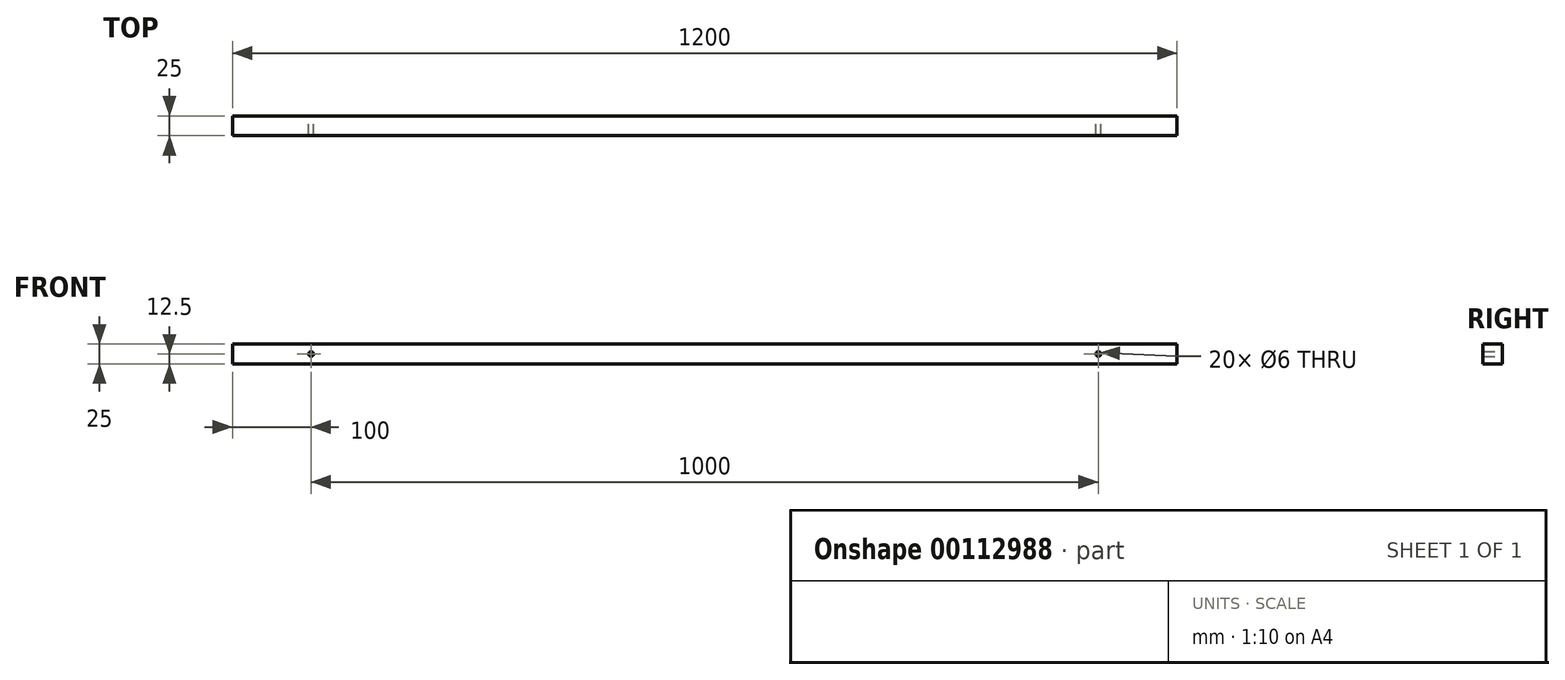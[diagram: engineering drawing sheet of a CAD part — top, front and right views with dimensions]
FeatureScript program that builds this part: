
annotation { "Feature Type Name" : "Feature", "Feature Type Description" : "" }
export const myFeature = defineFeature(function(context is Context, id is Id, definition is map)
    precondition{}
    {
        {
            var Q0;
            Q0=qCreatedBy(makeId("Front.planeOp"),FACE);
            var sketch = newSketch(context, id + "F0", { "sketchPlane" : qUnion([Q0])});
            skLineSegment(sketch, "E0.bottom", {"start": v(600, 12.5) * mm, "end": v(-600, 12.5) * mm});
            skLineSegment(sketch, "E0.top", {"start": v(600, -12.5) * mm, "end": v(-600, -12.5) * mm});
            skLineSegment(sketch, "E0.left", {"start": v(600, 12.5) * mm, "end": v(600, -12.5) * mm});
            skLineSegment(sketch, "E0.right", {"start": v(-600, 12.5) * mm, "end": v(-600, -12.5) * mm});
            skPoint(sketch, "E0.middle", {"position": v(0, 0) * mm});
            skCircle(sketch, "E1", {"center": v(-500, 0) * mm, "radius": 3 * mm});
            skCircle(sketch, "E2", {"center": v(500, 0) * mm, "radius": 3 * mm});
            skSolve(sketch);
        }
        {
            var Q0;
            Q0=makeQuery(id+"F0.imprint","IMPRINT",FACE,{"disambiguationData":[TD([[makeQuery(id+"F0.imprint","IMPRINT",EDGE,{"derivedFrom":sQuery(id+"F0.wireOp",EDGE,"E0.bottom")}),1.0]])]});
            extrude(context, id + "F1", {"entities" : qUnion([Q0]), "depth" : 25 * mm});
        }
    });
